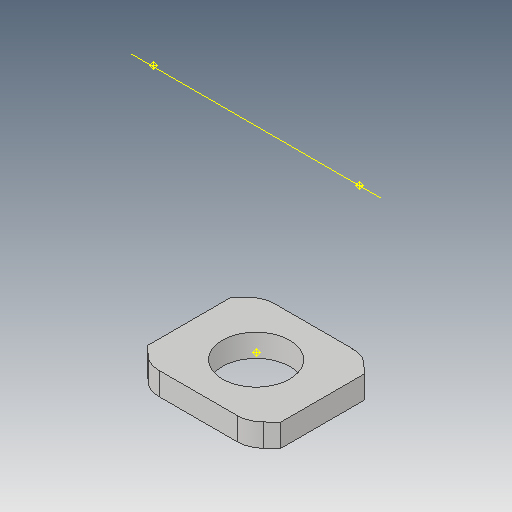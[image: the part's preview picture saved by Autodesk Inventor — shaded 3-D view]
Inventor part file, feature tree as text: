
AUTODESK INVENTOR PART (.ipt)
format: ipt  version: 2018 (Build 220112000, 112)  size: 717,312 bytes
history: native  units: mm
features: sketch x38, projected_geometry x37, extrude x33, other x10, chamfer x7, fillet x5, hole x3, reference x3, mirror x1, plane x1
ambient origin geometry x8: Origin, YZ Plane, XZ Plane, XY Plane, X Axis, Y Axis, Z Axis, Center Point
bodies: Solid1 (feature_tree)
feature tree (138):
  extrude  "Extrusion1"  Depth=45.0mm
  extrude  "Extrusion2"  Depth=2.25mm
  hole  "Hole1"  [1 undecoded]
  hole  "Hole2"  [1 undecoded]
  fillet  "Fillet1"  Radius=14.0mm
  extrude  "Extrusion3"  Depth=18.5mm
  extrude  "Extrusion4"  Depth=10.0mm
  extrude  "Extrusion5"  Depth=2.195mm
  extrude  "Extrusion6"  Depth=20.5mm
  hole  "Hole3"  [1 undecoded]
  extrude  "Extrusion7"  Depth=0.5mm
  extrude  "Extrusion8"  Depth=1.0mm TaperAngle=0.0deg
  extrude  "Extrusion9"  Depth=24.5mm
  extrude  "Extrusion10"  Depth=10.0mm
  extrude  "Extrusion11"  Depth=14.5mm
  extrude  "Extrusion13"  Depth=14.5mm
  extrude  "Extrusion14"  Depth=5.0mm
  extrude  "Extrusion15"  Depth=2.25mm
  extrude  "Extrusion16"  Depth=5.0mm
  extrude  "Extrusion17"  Depth=9.0mm
  chamfer  "Chamfer1"  Distance=1.0mm
  fillet  "Fillet7"  Radius=20.7mm
  fillet  "Fillet8"  Radius=32.0mm
  mirror  "Mirror1"
  sketch  "Sketch26"  dims[d55=2.25mm d56=5.0mm]
  extrude  "Extrusion24"  Depth=1.0mm TaperAngle=0.0deg
  extrude  "Extrusion25"  Depth=8.0mm
  extrude  "Extrusion26"  Depth=0.2mm TaperAngle=0.0deg
  extrude  "Extrusion27"  Depth=5.0mm TaperAngle=0.0deg
  other  "Work Axis1"
  plane  "Work Plane2"
  extrude  "Extrusion28"  Depth=0.2mm TaperAngle=0.0deg
  extrude  "Extrusion29"  Depth=2.5mm TaperAngle=45.0deg
  chamfer  "Chamfer2"  Distance=15.0mm
  extrude  "Extrusion31"  Depth=10.0mm TaperAngle=0.0deg
  chamfer  "Chamfer3"  Distance=15.0mm
  chamfer  "Chamfer4"  Distance=15.0mm
  extrude  "Extrusion32"  Depth=10.0mm
  chamfer  "Chamfer5"  Distance=41.5mm
  extrude  "Extrusion33"  Depth=10.0mm
  sketch  "Sketch41"  dims[d100=0.2mm d101=0.0mm d102=2.5mm d103=2.0mm d104=45.0deg]
  extrude  "Extrusion34"  Depth=10.0mm
  chamfer  "Chamfer6"  Distance=7.0mm
  fillet  "Fillet9"  Radius=100.0mm
  extrude  "Extrusion35"  Depth=10.0mm TaperAngle=0.0deg
  extrude  "Extrusion36"  Depth=10.0mm TaperAngle=45.0deg
  chamfer  "Chamfer7"  [1 undecoded]
  fillet  "Fillet10"  Radius=11.5mm
  extrude  "Extrusion37"  Depth=10.0mm
  extrude  "Extrusion38"  Depth=10.0mm
  extrude  "Extrusion40"  Depth=10.0mm TaperAngle=0.0deg
  extrude  "Extrusion41"  Depth=10.0mm TaperAngle=45.0deg
  extrude  "Extrusion42"  Depth=10.0mm TaperAngle=45.0deg
  sketch  "Sketch1"  dims[d0=24.5mm d1=45.0mm]
  sketch  "Sketch2"  dims[d2=1.95mm d3=0.0mm d4=2.25mm]
  projected_geometry  "Projected Loop1"
  sketch  "Sketch3"  dims[d5=20.0mm d6=2.25mm]
  projected_geometry  "Projected Loop2"
  sketch  "Sketch4"  dims[d7=5.25mm d8=5.25mm d9=14.0mm]
  projected_geometry  "Projected Loop3"
  sketch  "Sketch5"  dims[d10=5.25mm d11=18.5mm]
  projected_geometry  "Projected Loop4"
  sketch  "Sketch6"  dims[d12=10.0mm d13=0.0mm d14=20.5mm]
  projected_geometry  "Projected Loop5"
  sketch  "Sketch7"  dims[d15=2.0mm d16=2.195mm]
  projected_geometry  "Projected Loop6"
  sketch  "Sketch8"  dims[d17=2.0mm]
  projected_geometry  "Projected Loop7"
  sketch  "Sketch9"  dims[d18=2.4mm d19=6.0mm d20=4.4mm d21=2.0mm d22=90.0deg d23=8.0mm d24=20.594885mm d25=20.5mm]
  projected_geometry  "Projected Loop8"
  projected_geometry  "Projected Loop9"
  sketch  "Sketch10"  dims[d26=26.65mm d27=2.0mm]
  projected_geometry  "Projected Loop10"
  projected_geometry  "Projected Loop11"
  sketch  "Sketch11"  dims[d28=2.0mm]
  projected_geometry  "Projected Loop12"
  sketch  "Sketch12"  dims[d29=2.4mm d30=6.0mm d31=4.4mm d32=2.0mm d33=90.0deg d34=8.0mm d35=20.594885mm d36=0.5mm]
  sketch  "Sketch13"  dims[d37=18.0mm d38=1.0mm d39=0.0mm]
  sketch  "Sketch14"  dims[d41=5.0mm d42=0.0mm d43=24.5mm]
  projected_geometry  "Projected Loop13"
  sketch  "Sketch16"  dims[d44=1.15mm d45=0.0mm d46=10.0mm]
  projected_geometry  "Projected Loop14"
  sketch  "Sketch17"  dims[d47=21.0mm d48=14.5mm]
  projected_geometry  "Projected Loop15"
  sketch  "Sketch18"  dims[d49=20.0mm d50=14.5mm]
  projected_geometry  "Projected Loop16"
  sketch  "Sketch19"  dims[d51=24.5mm d52=5.0mm]
  projected_geometry  "Projected Loop17"
  sketch  "Sketch20"  dims[d53=5.0mm d54=2.25mm]
  projected_geometry  "Projected Loop18"
  projected_geometry  "Projected Loop25"
  sketch  "Sketch31"  dims[d57=5.0mm d58=9.0mm]
  projected_geometry  "Projected Loop30"
  reference  "Reference1"
  sketch  "Sketch32"  dims[d59=14.75mm]
  projected_geometry  "Projected Loop31"
  sketch  "Sketch33"  dims[d60=4.0mm d61=1.0mm d62=0.0mm d63=20.7mm]
  projected_geometry  "Projected Loop32"
  sketch  "Sketch34"  dims[d64=2.4mm d65=6.0mm d66=4.4mm d67=2.0mm d68=90.0deg d69=8.0mm d70=20.594885mm d72=32.0mm]
  projected_geometry  "Projected Loop33"
  other  "Work Point1"
  other  "Work Point2"
  other  "Work Point3"
  sketch  "Sketch35"  dims[d73=3.0mm d74=0.0mm d75=1.0mm d76=0.0mm]
  sketch  "Sketch37"  dims[d77=12.25mm d78=0.0mm d80=8.0mm]
  projected_geometry  "Projected Loop34"
  sketch  "Sketch38"  dims[d81=4.5mm d82=0.0mm d84=0.2mm d85=0.0mm]
  sketch  "Sketch39"  dims[d91=8.0mm d92=0.0mm d93=5.0mm d94=0.0mm]
  sketch  "Sketch40"  dims[d95=5.0mm d96=0.0mm d98=0.2mm d99=0.0mm]
  projected_geometry  "Projected Loop35"
  projected_geometry  "Projected Loop36"
  projected_geometry  "Projected Loop37"
  projected_geometry  "Projected Loop38"
  sketch  "Sketch42"  dims[d105=1.5mm]
  projected_geometry  "Projected Loop39"
  sketch  "Sketch43"  dims[d114=0.5mm]
  reference  "Reference2"
  reference  "Reference3"
  sketch  "Sketch45"  dims[d130=60.0mm]
  projected_geometry  "Projected Loop40"
  sketch  "Sketch46"  dims[d131=36.0mm]
  projected_geometry  "Projected Loop41"
  sketch  "Sketch48"  dims[d146=40.0mm]
  projected_geometry  "Projected Loop43"
  sketch  "Sketch50"  dims[d147=60.0mm]
  projected_geometry  "Projected Loop46"
  sketch  "Sketch53"  dims[d148=0.0mm]
  projected_geometry  "Projected Loop48"
  sketch  "Sketch55"  dims[d149=2.3mm d150=15.0mm d151=0.0mm d152=15.0mm d153=0.0mm d154=15.0mm d155=0.0mm d156=15.0mm d157=0.0mm d158=20.5mm d159=41.5mm d160=14.0mm d161=14.0mm d162=7.0mm d165=100.0mm d166=0.0mm d167=100.0mm d168=0.0mm d169=6.0mm d170=2.0mm d171=45.0deg d172=0.0mm d173=11.5mm d175=11.5mm d176=11.5mm d179=100.0mm d180=0.0mm d181=5.0mm d182=2.0mm d183=45.0deg d184=5.0mm d185=2.0mm d186=45.0deg d187=8.0mm d188=100.0mm d189=0.0mm d190=5.0mm d191=2.0mm d192=45.0deg d193=100.0mm d194=0.0mm d195=100.0mm d196=0.0mm d197=5.0mm d198=2.0mm d199=45.0deg d200=8.0mm d202=15.0deg d204=10.970628mm d205=15.470628mm d206=2.5mm d207=0.0mm d208=2.5mm d209=0.0mm d210=3.0mm d211=2.0mm d212=45.0deg d213=2.0mm d215=15.0deg d216=4.0mm d217=4.0mm d218=5.0mm d219=0.0mm d222=32.07mm d223=3.9mm d224=0.0mm d227=7.1mm d228=0.0mm d237=10.0mm d238=0.0mm d239=10.0mm d240=0.0mm]
  projected_geometry  "Projected Loop49"
  parser-record x1  (decoder bookkeeping rows leaked as tree rows — omitted from the tree; the rows remain in map.json)
  other  "servocheck.iam"
  other  "LX-16A:3"
  other  "DUOPAN-SG-SJ_10"
  projected_geometry  "Project Cut Edges1"
  projected_geometry  "Project Cut Edges3"
  other  "bottomarm:1"
  other  "arm1:1"
note: 4 required parameter values undecoded (feature->parameter linkage not recoverable at this tier; creation-order binding heuristic only, values carry confidence <= 0.55)
note: 1 file-system path scrubbed to <path> (originals preserved in map.json)
